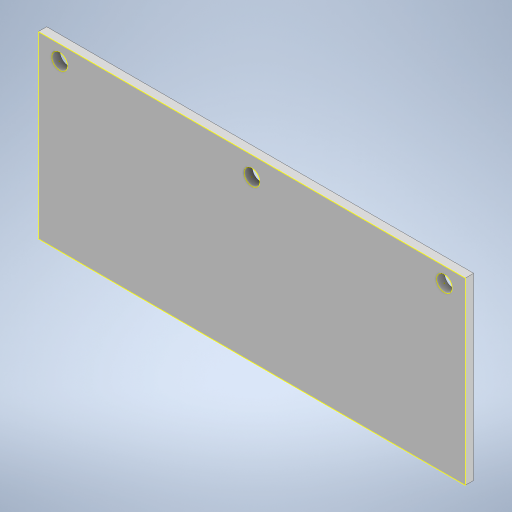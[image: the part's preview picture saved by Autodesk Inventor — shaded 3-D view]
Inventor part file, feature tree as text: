
AUTODESK INVENTOR PART (.ipt)
format: ipt  version: 2023 (Build 270158000, 158)  size: 230,912 bytes
history: native  units: in
note: dims shown in document units (in); Inventor stores cm internally (conversion verified against a paired STEP export)
features: reference x10, other x6, sketch x4, extrude x3, projected_geometry x2
ambient origin geometry x8: Origin, YZ Plane, XZ Plane, XY Plane, X Axis, Y Axis, Z Axis, Center Point
bodies: Body1 (feature_tree)
feature tree (25):
  other  "Bryła1"
  extrude  "Wyciągnięcie proste1"  Depth=0.0984in
  extrude  "Wyciągnięcie proste2"  Depth=0.063in TaperAngle=0.0deg
  extrude  "Wyciągnięcie proste3"  TaperAngle=0.0deg  [1 undecoded]
  sketch  "Szkic5"
  sketch  "Szkic1"
  reference  "Odniesienie1"
  reference  "Odniesienie2"
  reference  "Odniesienie3"
  reference  "Odniesienie4"
  reference  "Odniesienie5"
  reference  "Odniesienie6"
  reference  "Odniesienie7"
  reference  "Odniesienie8"
  sketch  "Szkic2"
  reference  "Odniesienie9"
  reference  "Odniesienie10"
  sketch  "Szkic3"
  projected_geometry  "Pętla rzutowana1"
  projected_geometry  "Pętla rzutowana3"
  other  "<userpath>\Desktop\MojeRoboty\Stefan\mechanics\STEFAN_2.0.iam"
  other  "STEFAN_2.0.iam"
  other  "mocowanie_serw:1"
  other  "SCIANA_2.0_MIR:1"
  other  "SCIANA_2.0:1"
note: 1 required parameter value undecoded (feature->parameter linkage not recoverable at this tier; creation-order binding heuristic only, values carry confidence <= 0.55)
